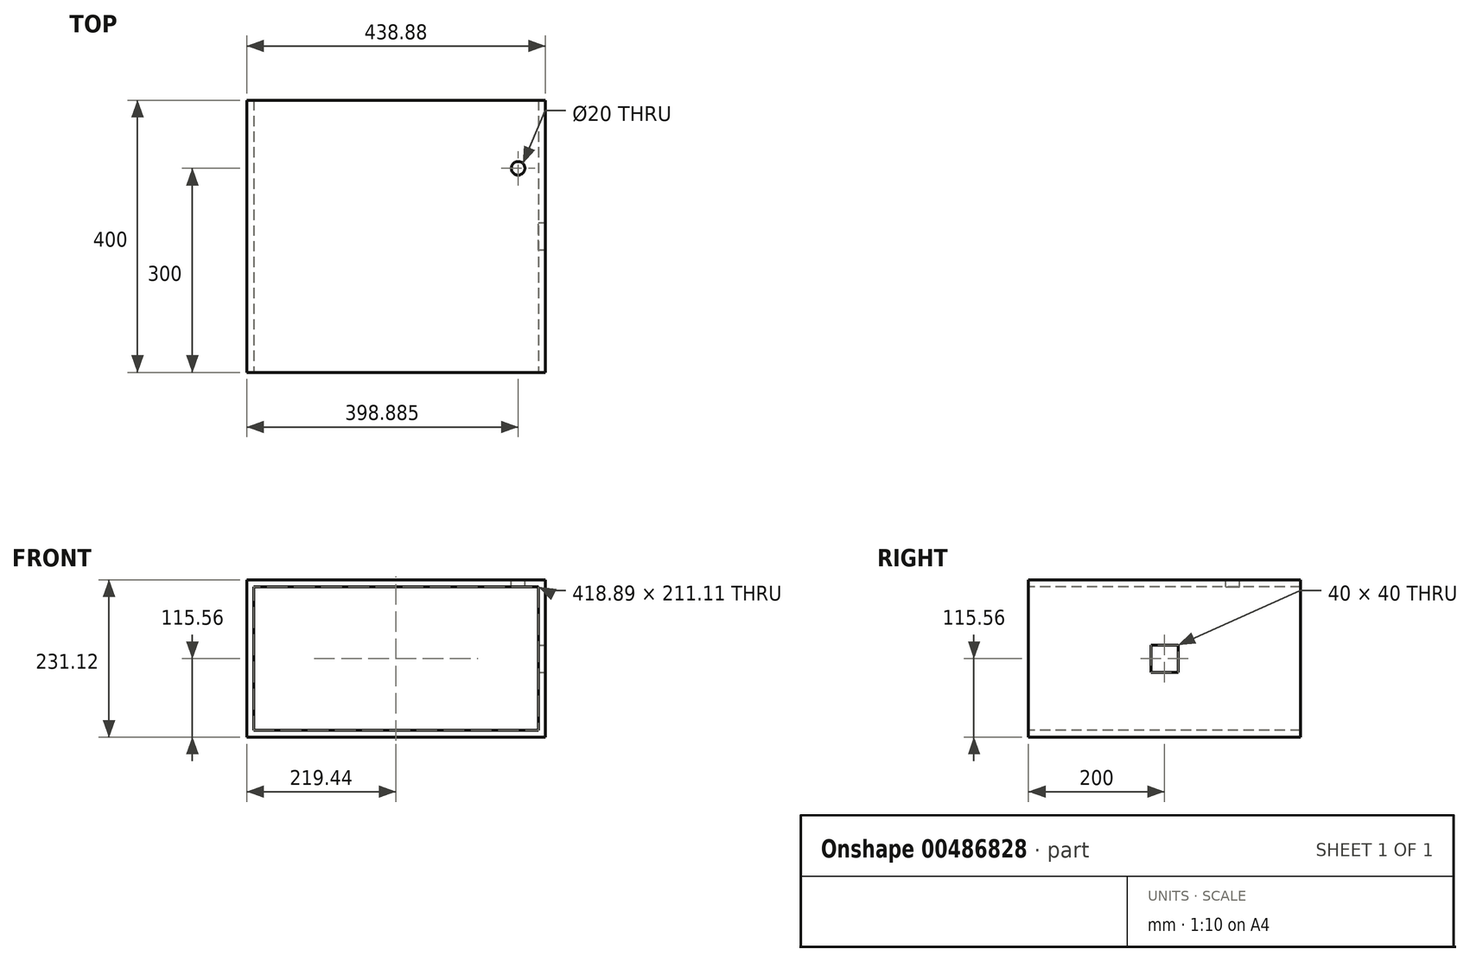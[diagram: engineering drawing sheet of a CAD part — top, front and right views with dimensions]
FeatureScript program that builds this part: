
annotation { "Feature Type Name" : "Feature", "Feature Type Description" : "" }
export const myFeature = defineFeature(function(context is Context, id is Id, definition is map)
    precondition{}
    {
        {
            var Q0;
            Q0=qCreatedBy(makeId("Front.planeOp"),FACE);
            var sketch = newSketch(context, id + "F0", { "sketchPlane" : qUnion([Q0])});
            skLineSegment(sketch, "E0.bottom", {"start": v(209.44, -105.56) * mm, "end": v(-209.44, -105.56) * mm});
            skLineSegment(sketch, "E0.top", {"start": v(209.44, 105.56) * mm, "end": v(-209.44, 105.56) * mm});
            skLineSegment(sketch, "E0.left", {"start": v(209.44, -105.56) * mm, "end": v(209.44, 105.56) * mm});
            skLineSegment(sketch, "E0.right", {"start": v(-209.44, -105.56) * mm, "end": v(-209.44, 105.56) * mm});
            skPoint(sketch, "E0.middle", {"position": v(0, 0) * mm});
            skLineSegment(sketch, "E1.bottom", {"start": v(219.44, -115.56) * mm, "end": v(-219.44, -115.56) * mm});
            skLineSegment(sketch, "E1.top", {"start": v(219.44, 115.56) * mm, "end": v(-219.44, 115.56) * mm});
            skLineSegment(sketch, "E1.left", {"start": v(219.44, -115.56) * mm, "end": v(219.44, 115.56) * mm});
            skLineSegment(sketch, "E1.right", {"start": v(-219.44, -115.56) * mm, "end": v(-219.44, 115.56) * mm});
            skSolve(sketch);
        }
        {
            var Q0;
            Q0=makeQuery(id+"F0.imprint","IMPRINT",FACE,{"disambiguationData":[TD([[makeQuery(id+"F0.imprint","IMPRINT",EDGE,{"derivedFrom":sQuery(id+"F0.wireOp",EDGE,"E0.bottom")}),1.0]])]});
            extrude(context, id + "F1", {"entities" : qUnion([Q0]), "oppositeDirection" : true, "depth" : 400 * mm});
        }
        {
            var Q0;
            Q0=makeQuery(id+"F1.opExtrude","SWEPT_FACE",FACE,{"disambiguationData":[OSD([sQuery(id+"F0.wireOp",EDGE,"E1.top")])]});
            var sketch = newSketch(context, id + "F2", { "sketchPlane" : qUnion([Q0])});
            skCircle(sketch, "E2", {"center": v(179.44, 300) * mm, "radius": 15 * mm});
            skSolve(sketch);
        }
        {
            var Q0;
            Q0=sQuery(id+"F2.wireOp",VERTEX,"E2.center");
            var Q1;
            Q1=makeQuery(id+"F1.opExtrude","SWEPT_BODY",BODY,{"disambiguationData":[OSD([sQuery(id+"F0.wireOp",EDGE,"E0.bottom"),sQuery(id+"F0.wireOp",EDGE,"E0.top"),sQuery(id+"F0.wireOp",EDGE,"E0.left"),sQuery(id+"F0.wireOp",EDGE,"E0.right"),sQuery(id+"F0.wireOp",EDGE,"E1.bottom"),sQuery(id+"F0.wireOp",EDGE,"E1.top"),sQuery(id+"F0.wireOp",EDGE,"E1.left"),sQuery(id+"F0.wireOp",EDGE,"E1.right")])]});
            hole(context, id + "F3", {"style" : HoleStyle.SIMPLE, "endStyle" : HoleEndStyle.BLIND, "holeDiameter" : 20 * mm, "holeDepth" : 12.4 * mm, "isTappedThrough" : true, "tappedDepth" : 10 * mm, "tapClearance" : 3, "locations" : qUnion([Q0]), "scope" : qUnion([Q1])});
        }
        {
            var Q0;
            Q0=makeQuery(id+"F1.opExtrude","SWEPT_FACE",FACE,{"disambiguationData":[OSD([sQuery(id+"F0.wireOp",EDGE,"E1.left")])]});
            var sketch = newSketch(context, id + "F4", { "sketchPlane" : qUnion([Q0])});
            skLineSegment(sketch, "E3", {"start": v(200, -115.56) * mm, "end": v(200, 115.56) * mm, "construction": true});
            skLineSegment(sketch, "E4.bottom", {"start": v(220, -20) * mm, "end": v(180, -20) * mm});
            skLineSegment(sketch, "E4.top", {"start": v(220, 20) * mm, "end": v(180, 20) * mm});
            skLineSegment(sketch, "E4.left", {"start": v(220, -20) * mm, "end": v(220, 20) * mm});
            skLineSegment(sketch, "E4.right", {"start": v(180, -20) * mm, "end": v(180, 20) * mm});
            skPoint(sketch, "E4.middle", {"position": v(200, 0) * mm});
            skLineSegment(sketch, "E5", {"start": v(0, 0) * mm, "end": v(400, 0) * mm, "construction": true});
            skSolve(sketch);
        }
        {
            var Q0;
            Q0=makeQuery(id+"F4.imprint","IMPRINT",FACE,{"disambiguationData":[TD([[makeQuery(id+"F4.imprint","IMPRINT",EDGE,{"derivedFrom":sQuery(id+"F4.wireOp",EDGE,"E4.bottom")}),-1.0]])]});
            extrude(context, id + "F5", {"entities" : qUnion([Q0]), "operationType" : NewBodyOperationType.REMOVE, "endBound" : BoundingType.UP_TO_NEXT, "oppositeDirection" : true, "depth" : 25 * mm});
        }
    });
